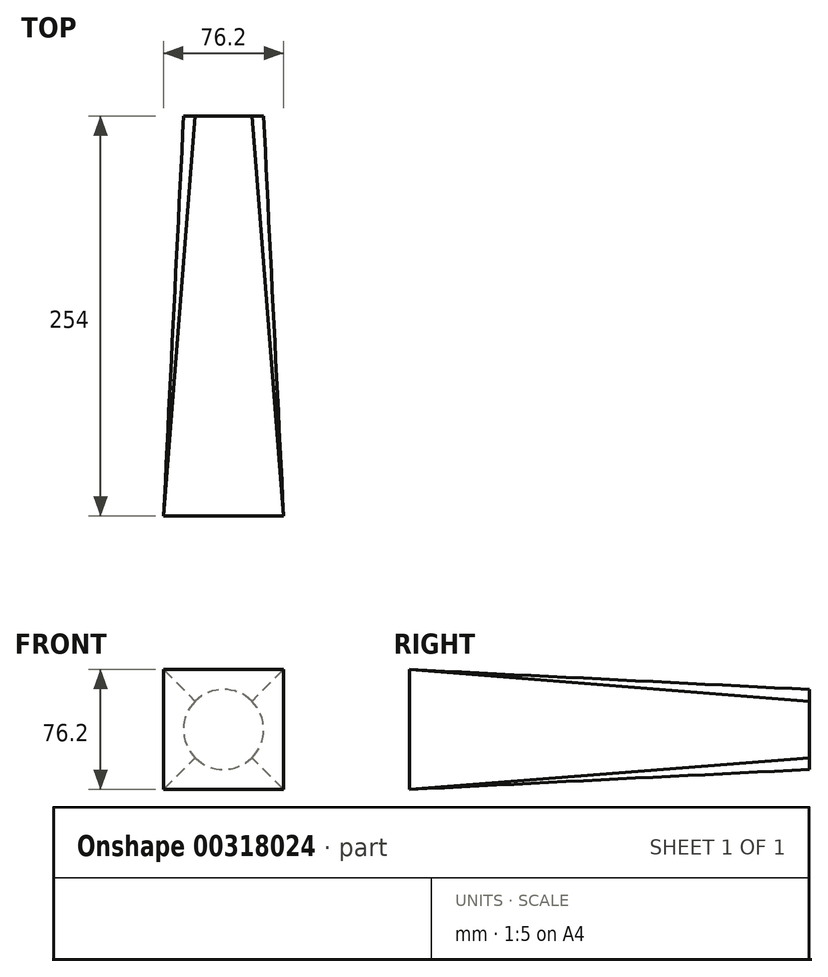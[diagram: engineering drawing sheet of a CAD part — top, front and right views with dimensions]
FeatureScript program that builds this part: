
annotation { "Feature Type Name" : "Feature", "Feature Type Description" : "" }
export const myFeature = defineFeature(function(context is Context, id is Id, definition is map)
    precondition{}
    {
        {
            var Q0;
            Q0=qCreatedBy(makeId("Front.planeOp"),FACE);
            var sketch = newSketch(context, id + "F0", { "sketchPlane" : qUnion([Q0])});
            skLineSegment(sketch, "E0.bottom", {"start": v(38.1, 38.1) * mm, "end": v(-38.1, 38.1) * mm});
            skLineSegment(sketch, "E0.top", {"start": v(38.1, -38.1) * mm, "end": v(-38.1, -38.1) * mm});
            skLineSegment(sketch, "E0.left", {"start": v(38.1, 38.1) * mm, "end": v(38.1, -38.1) * mm});
            skLineSegment(sketch, "E0.right", {"start": v(-38.1, 38.1) * mm, "end": v(-38.1, -38.1) * mm});
            skPoint(sketch, "E0.middle", {"position": v(0, 0) * mm});
            skSolve(sketch);
        }
        {
            var Q0;
            Q0=qCreatedBy(makeId("Front.planeOp"),FACE);
            cPlane(context, id + "F1", {"entities" : qUnion([Q0]), "cplaneType" : CPlaneType.OFFSET, "offset" : 254 * mm, "oppositeDirection" : true, "width" : 152.4 * mm, "height" : 152.4 * mm});
        }
        {
            var Q0;
            Q0=qCreatedBy(id+"F1.planeOp",FACE);
            var sketch = newSketch(context, id + "F2", { "sketchPlane" : qUnion([Q0])});
            skCircle(sketch, "E1", {"center": v(0, 0) * mm, "radius": 25.4 * mm});
            skSolve(sketch);
        }
        {
            var Q0;
            Q0=makeQuery(id+"F0.imprint","IMPRINT",FACE,{"disambiguationData":[TD([[makeQuery(id+"F0.imprint","IMPRINT",EDGE,{"derivedFrom":sQuery(id+"F0.wireOp",EDGE,"E0.bottom")}),1.0]])]});
            var Q1;
            Q1=makeQuery(id+"F2.imprint","IMPRINT",FACE,{"disambiguationData":[TD([[makeQuery(id+"F2.imprint","IMPRINT",EDGE,{"derivedFrom":sQuery(id+"F2.wireOp",EDGE,"E1")}),1.0]])]});
            loft(context, id + "F3", {"sheetProfilesArray" : [{ "sheetProfileEntities" : qUnion([Q0]) }, { "sheetProfileEntities" : qUnion([Q1]) }]});
        }
    });
